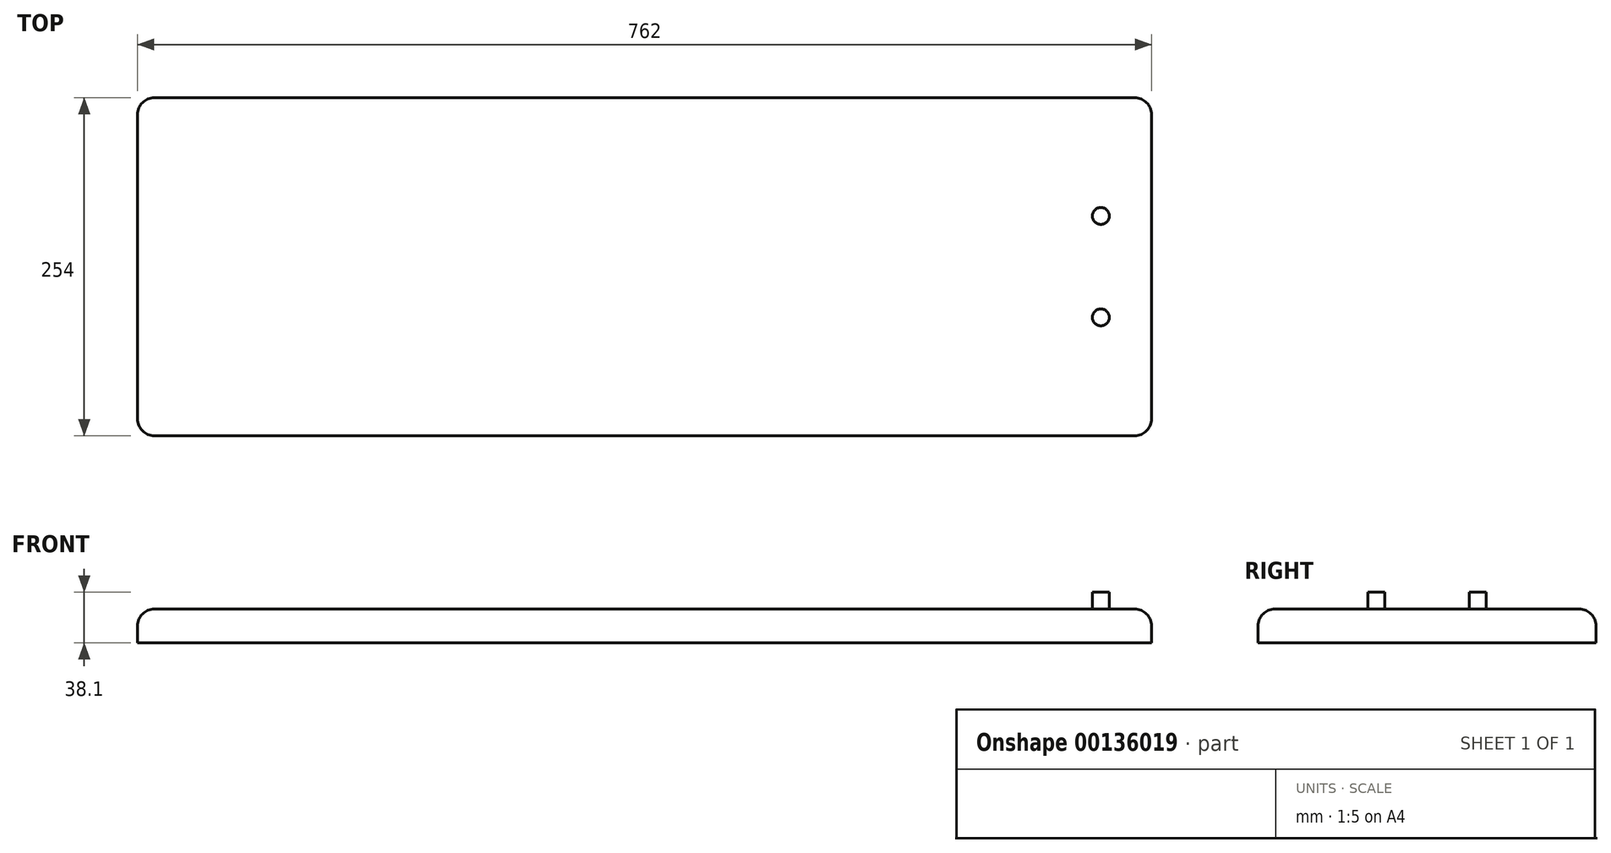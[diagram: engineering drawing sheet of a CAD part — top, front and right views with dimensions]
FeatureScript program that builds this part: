
annotation { "Feature Type Name" : "Feature", "Feature Type Description" : "" }
export const myFeature = defineFeature(function(context is Context, id is Id, definition is map)
    precondition{}
    {
        {
            var Q0;
            Q0=qCreatedBy(makeId("Top.planeOp"),FACE);
            var sketch = newSketch(context, id + "F0", { "sketchPlane" : qUnion([Q0])});
            skLineSegment(sketch, "E0.bottom", {"start": v(0, 0) * mm, "end": v(-762, 0) * mm});
            skLineSegment(sketch, "E0.top", {"start": v(0, -254) * mm, "end": v(-762, -254) * mm});
            skLineSegment(sketch, "E0.left", {"start": v(0, 0) * mm, "end": v(0, -254) * mm});
            skLineSegment(sketch, "E0.right", {"start": v(-762, 0) * mm, "end": v(-762, -254) * mm});
            skSolve(sketch);
        }
        {
            var Q0;
            Q0=makeQuery(id+"F0.imprint","IMPRINT",FACE,{"disambiguationData":[TD([[makeQuery(id+"F0.imprint","IMPRINT",EDGE,{"derivedFrom":sQuery(id+"F0.wireOp",EDGE,"E0.bottom")}),1.0]])]});
            extrude(context, id + "F1", {"entities" : qUnion([Q0]), "depth" : 25.4 * mm});
        }
        {
            var Q0;
            Q0=makeQuery(id+"F1.opExtrude","CAP_EDGE",EDGE,{"disambiguationData":[OSD([sQuery(id+"F0.wireOp",EDGE,"E0.left")])],"isStart":false});
            var Q1;
            Q1=makeQuery(id+"F1.opExtrude","CAP_EDGE",EDGE,{"disambiguationData":[OSD([sQuery(id+"F0.wireOp",EDGE,"E0.top")])],"isStart":false});
            var Q2;
            Q2=makeQuery(id+"F1.opExtrude","CAP_EDGE",EDGE,{"disambiguationData":[OSD([sQuery(id+"F0.wireOp",EDGE,"E0.bottom")])],"isStart":false});
            var Q3;
            Q3=makeQuery(id+"F1.opExtrude","CAP_EDGE",EDGE,{"disambiguationData":[OSD([sQuery(id+"F0.wireOp",EDGE,"E0.right")])],"isStart":false});
            fillet(context, id + "F2", {"entities" : qUnion([Q0, Q1, Q2, Q3]), "radius" : 12.7 * mm, "tangentPropagation" : true, "allowEdgeOverflow" : false});
        }
        {
            var Q0;
            Q0=makeQuery(id+"F1.opExtrude","SWEPT_EDGE",EDGE,{"disambiguationData":[OSD([sQuery(id+"F0.wireOp",EDGE,"E0.top"),sQuery(id+"F0.wireOp",EDGE,"E0.right")])]});
            var Q1;
            Q1=makeQuery(id+"F2.opFillet","BLEND_EDGE",EDGE,{"blendedFrom":[makeQuery(id+"F1.opExtrude","CAP_EDGE",EDGE,{"disambiguationData":[OSD([sQuery(id+"F0.wireOp",EDGE,"E0.top")])],"isStart":false}),makeQuery(id+"F1.opExtrude","CAP_EDGE",EDGE,{"disambiguationData":[OSD([sQuery(id+"F0.wireOp",EDGE,"E0.right")])],"isStart":false})],"blendedInto":[]});
            var Q2;
            Q2=makeQuery(id+"F2.opFillet","BLEND_EDGE",EDGE,{"blendedFrom":[makeQuery(id+"F1.opExtrude","CAP_EDGE",EDGE,{"disambiguationData":[OSD([sQuery(id+"F0.wireOp",EDGE,"E0.bottom")])],"isStart":false}),makeQuery(id+"F1.opExtrude","CAP_EDGE",EDGE,{"disambiguationData":[OSD([sQuery(id+"F0.wireOp",EDGE,"E0.right")])],"isStart":false})],"blendedInto":[]});
            var Q3;
            Q3=makeQuery(id+"F2.opFillet","BLEND_EDGE",EDGE,{"blendedFrom":[makeQuery(id+"F1.opExtrude","CAP_EDGE",EDGE,{"disambiguationData":[OSD([sQuery(id+"F0.wireOp",EDGE,"E0.bottom")])],"isStart":false}),makeQuery(id+"F1.opExtrude","CAP_EDGE",EDGE,{"disambiguationData":[OSD([sQuery(id+"F0.wireOp",EDGE,"E0.left")])],"isStart":false})],"blendedInto":[]});
            var Q4;
            Q4=makeQuery(id+"F2.opFillet","BLEND_EDGE",EDGE,{"blendedFrom":[makeQuery(id+"F1.opExtrude","CAP_EDGE",EDGE,{"disambiguationData":[OSD([sQuery(id+"F0.wireOp",EDGE,"E0.top")])],"isStart":false}),makeQuery(id+"F1.opExtrude","CAP_EDGE",EDGE,{"disambiguationData":[OSD([sQuery(id+"F0.wireOp",EDGE,"E0.left")])],"isStart":false})],"blendedInto":[]});
            fillet(context, id + "F3", {"entities" : qUnion([Q0, Q1, Q2, Q3, Q4]), "radius" : 12.7 * mm, "tangentPropagation" : true, "allowEdgeOverflow" : false});
        }
        {
            var Q0;
            Q0=makeQuery(id+"F1.opExtrude","CAP_FACE",FACE,{"disambiguationData":[OSD([sQuery(id+"F0.wireOp",EDGE,"E0.bottom"),sQuery(id+"F0.wireOp",EDGE,"E0.top"),sQuery(id+"F0.wireOp",EDGE,"E0.left"),sQuery(id+"F0.wireOp",EDGE,"E0.right")])],"isStart":false});
            var sketch = newSketch(context, id + "F4", { "sketchPlane" : qUnion([Q0])});
            skLineSegment(sketch, "E1.bottom", {"start": v(-12.7, -241.3) * mm, "end": v(-241.3, -241.3) * mm});
            skLineSegment(sketch, "E1.top", {"start": v(-12.7, -12.7) * mm, "end": v(-241.3, -12.7) * mm});
            skLineSegment(sketch, "E1.left", {"start": v(-12.7, -241.3) * mm, "end": v(-12.7, -12.7) * mm});
            skLineSegment(sketch, "E1.right", {"start": v(-241.3, -241.3) * mm, "end": v(-241.3, -12.7) * mm});
            skLineSegment(sketch, "E2.bottom", {"start": v(-12.7, -165.1) * mm, "end": v(-114.3, -165.1) * mm});
            skLineSegment(sketch, "E2.top", {"start": v(-12.7, -88.9) * mm, "end": v(-114.3, -88.9) * mm});
            skLineSegment(sketch, "E2.left", {"start": v(-12.7, -165.1) * mm, "end": v(-12.7, -88.9) * mm});
            skLineSegment(sketch, "E2.right", {"start": v(-114.3, -165.1) * mm, "end": v(-114.3, -88.9) * mm});
            skLineSegment(sketch, "E3.bottom", {"start": v(-114.3, -88.9) * mm, "end": v(-38.1, -88.9) * mm});
            skLineSegment(sketch, "E3.top", {"start": v(-114.3, -165.1) * mm, "end": v(-38.1, -165.1) * mm});
            skLineSegment(sketch, "E3.left", {"start": v(-114.3, -88.9) * mm, "end": v(-114.3, -165.1) * mm});
            skLineSegment(sketch, "E3.right", {"start": v(-38.1, -88.9) * mm, "end": v(-38.1, -165.1) * mm});
            skCircle(sketch, "E4", {"center": v(-114.3, -165.1) * mm, "radius": 6.35 * mm});
            skCircle(sketch, "E5", {"center": v(-114.3, -88.9) * mm, "radius": 6.35 * mm});
            skCircle(sketch, "E6", {"center": v(-38.1, -88.9) * mm, "radius": 6.35 * mm});
            skCircle(sketch, "E7", {"center": v(-38.1, -165.1) * mm, "radius": 6.35 * mm});
            skSolve(sketch);
        }
        {
            var Q0;
            {var subQ1=sQuery(id+"F4.wireOp",EDGE,"E3.top");var subQ3=sQuery(id+"F4.wireOp",EDGE,"E7");var subQ4=makeQuery(id+"F4.imprint","INTERSECT",VERTEX,{"derivedFrom":[subQ1,subQ3]});Q0=makeQuery(id+"F4.imprint","IMPRINT",FACE,{"disambiguationData":[TD([[makeQuery(id+"F4.imprint","IMPRINT",EDGE,{"disambiguationData":[TD([[subQ4,1.0]])],"derivedFrom":subQ3}),1.0]])]});}
            var Q1;
            {var subQ1=sQuery(id+"F4.wireOp",EDGE,"E2.bottom");var subQ3=sQuery(id+"F4.wireOp",EDGE,"E7");var subQ4=makeQuery(id+"F4.imprint","INTERSECT",VERTEX,{"derivedFrom":[subQ1,subQ3]});Q1=makeQuery(id+"F4.imprint","IMPRINT",FACE,{"disambiguationData":[TD([[makeQuery(id+"F4.imprint","IMPRINT",EDGE,{"disambiguationData":[TD([[subQ4,1.0]])],"derivedFrom":subQ3}),1.0]])]});}
            var Q2;
            {var subQ1=sQuery(id+"F4.wireOp",EDGE,"E2.bottom");var subQ3=sQuery(id+"F4.wireOp",EDGE,"E7");var subQ4=makeQuery(id+"F4.imprint","INTERSECT",VERTEX,{"derivedFrom":[subQ1,subQ3]});Q2=makeQuery(id+"F4.imprint","IMPRINT",FACE,{"disambiguationData":[TD([[makeQuery(id+"F4.imprint","IMPRINT",EDGE,{"disambiguationData":[TD([[subQ4,-1.0]])],"derivedFrom":subQ3}),1.0]])]});}
            var Q3;
            {var subQ0=sQuery(id+"F4.wireOp",EDGE,"E3.left");var subQ1=sQuery(id+"F4.wireOp",EDGE,"E3.top");var subQ2=makeQuery(id+"F4.imprint","INTERSECT",VERTEX,{"derivedFrom":[subQ1,subQ0]});Q3=makeQuery(id+"F4.imprint","IMPRINT",FACE,{"disambiguationData":[TD([[makeQuery(id+"F4.imprint","IMPRINT",EDGE,{"disambiguationData":[TD([[subQ2,-1.0]])],"derivedFrom":subQ1}),-1.0]])]});}
            var Q4;
            {var subQ0=sQuery(id+"F4.wireOp",EDGE,"E3.left");var subQ1=sQuery(id+"F4.wireOp",EDGE,"E3.top");var subQ2=makeQuery(id+"F4.imprint","INTERSECT",VERTEX,{"derivedFrom":[subQ1,subQ0]});Q4=makeQuery(id+"F4.imprint","IMPRINT",FACE,{"disambiguationData":[TD([[makeQuery(id+"F4.imprint","IMPRINT",EDGE,{"disambiguationData":[TD([[subQ2,-1.0]])],"derivedFrom":subQ1}),1.0]])]});}
            var Q5;
            {var subQ0=sQuery(id+"F4.wireOp",EDGE,"E3.left");var subQ1=sQuery(id+"F4.wireOp",EDGE,"E3.bottom");var subQ2=makeQuery(id+"F4.imprint","INTERSECT",VERTEX,{"derivedFrom":[subQ1,subQ0]});Q5=makeQuery(id+"F4.imprint","IMPRINT",FACE,{"disambiguationData":[TD([[makeQuery(id+"F4.imprint","IMPRINT",EDGE,{"disambiguationData":[TD([[subQ2,-1.0]])],"derivedFrom":subQ1}),1.0]])]});}
            var Q6;
            {var subQ0=sQuery(id+"F4.wireOp",EDGE,"E3.left");var subQ1=sQuery(id+"F4.wireOp",EDGE,"E3.bottom");var subQ2=makeQuery(id+"F4.imprint","INTERSECT",VERTEX,{"derivedFrom":[subQ1,subQ0]});Q6=makeQuery(id+"F4.imprint","IMPRINT",FACE,{"disambiguationData":[TD([[makeQuery(id+"F4.imprint","IMPRINT",EDGE,{"disambiguationData":[TD([[subQ2,-1.0]])],"derivedFrom":subQ1}),-1.0]])]});}
            var Q7;
            {var subQ1=sQuery(id+"F4.wireOp",EDGE,"E2.top");var subQ3=sQuery(id+"F4.wireOp",EDGE,"E6");var subQ4=makeQuery(id+"F4.imprint","INTERSECT",VERTEX,{"derivedFrom":[subQ1,subQ3]});Q7=makeQuery(id+"F4.imprint","IMPRINT",FACE,{"disambiguationData":[TD([[makeQuery(id+"F4.imprint","IMPRINT",EDGE,{"disambiguationData":[TD([[subQ4,-1.0]])],"derivedFrom":subQ3}),1.0]])]});}
            var Q8;
            {var subQ1=sQuery(id+"F4.wireOp",EDGE,"E3.bottom");var subQ3=sQuery(id+"F4.wireOp",EDGE,"E6");var subQ4=makeQuery(id+"F4.imprint","INTERSECT",VERTEX,{"derivedFrom":[subQ1,subQ3]});Q8=makeQuery(id+"F4.imprint","IMPRINT",FACE,{"disambiguationData":[TD([[makeQuery(id+"F4.imprint","IMPRINT",EDGE,{"disambiguationData":[TD([[subQ4,-1.0]])],"derivedFrom":subQ3}),1.0]])]});}
            var Q9;
            {var subQ1=sQuery(id+"F4.wireOp",EDGE,"E2.top");var subQ3=sQuery(id+"F4.wireOp",EDGE,"E6");var subQ4=makeQuery(id+"F4.imprint","INTERSECT",VERTEX,{"derivedFrom":[subQ1,subQ3]});Q9=makeQuery(id+"F4.imprint","IMPRINT",FACE,{"disambiguationData":[TD([[makeQuery(id+"F4.imprint","IMPRINT",EDGE,{"disambiguationData":[TD([[subQ4,1.0]])],"derivedFrom":subQ3}),1.0]])]});}
            extrude(context, id + "F5", {"entities" : qUnion([Q0, Q1, Q2, Q3, Q4, Q5, Q6, Q7, Q8, Q9]), "operationType" : NewBodyOperationType.ADD, "depth" : 12.7 * mm});
        }
    });
